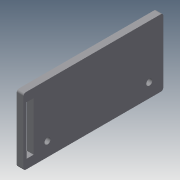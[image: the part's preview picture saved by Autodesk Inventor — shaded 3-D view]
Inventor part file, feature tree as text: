
AUTODESK INVENTOR PART (.ipt)
format: ipt  version: 2014 (Build 180170000, 170)  size: 93,184 bytes
history: native  units: mm
features: extrude x1, fillet x1, sketch x1
ambient origin geometry x8: Origin, YZ Plane, XZ Plane, XY Plane, X Axis, Y Axis, Z Axis, Center Point
bodies: Solid1 (feature_tree)
feature tree (3):
  extrude  "Extrusion1"  Depth=125.0mm
  fillet  "Fillet1"  Radius=6.25mm
  sketch  "Sketch1"  dims[d0=60.0mm d1=125.0mm d2=6.25mm d3=2.875mm d4=8.1mm d5=8.1mm d6=12.5mm d7=21.5mm d8=12.5mm d9=5.4mm d10=6.0mm d11=0.0mm d12=2.0mm]
